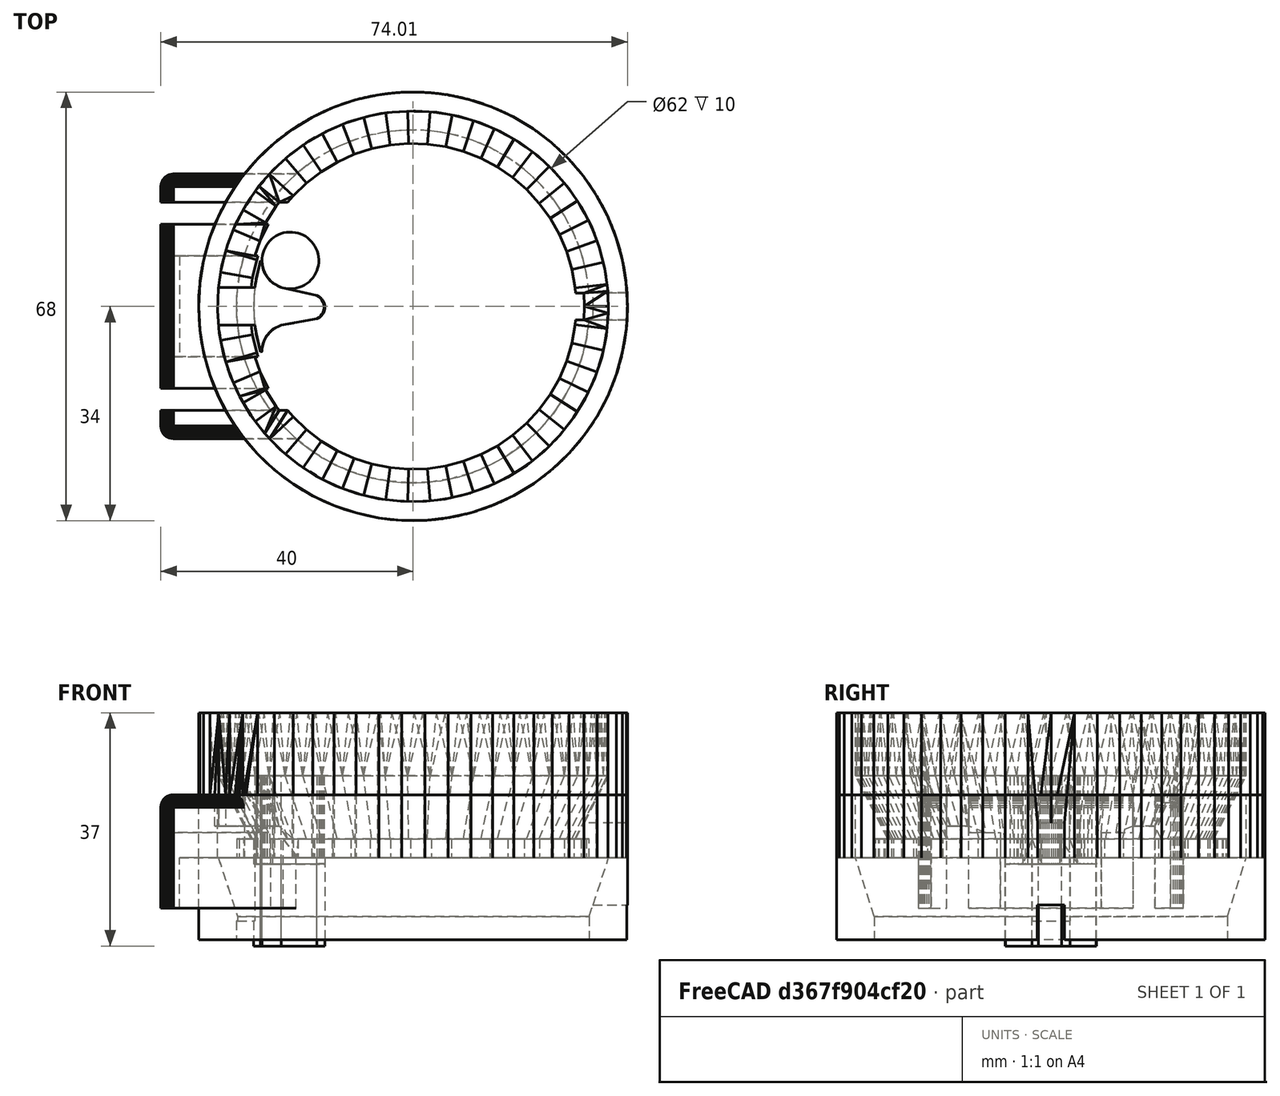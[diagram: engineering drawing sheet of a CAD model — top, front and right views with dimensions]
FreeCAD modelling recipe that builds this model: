
FCSTD DOCUMENT  (FreeCAD 0.20R29177 +426 (Git))
Label: lid
License: All rights reserved
LicenseURL: http://en.wikipedia.org/wiki/All_rights_reserved
objects: Part::MultiFuse×3, Part::Cylinder×3, Part::Cut×3, Part::Box×2, Mesh::Feature×1, Sketcher::SketchObject×1, Part::Extrusion×1, Part::FeaturePython×1, Part::Cone×1, Part::Feature×1
note: 16 computed .brp shape members not serialized (recipe doc carries the construction recipe); baked Part::Feature solids carry a one-line shape summary decoded from their .brp

FEATURE [Mesh::Feature] Lid_V5  label="Lid V5"
FEATURE [Part::Box] Box012  label="Cube012"
  AttacherType = Attacher::AttachEngine3D
  Height = 10
  Length = 10
  Placement = pos=(7,36.17,76) rot=(0,0,1;0rad)
  Width = 6
FEATURE [Sketcher::SketchObject] Sketch
  FullyConstrained = true
  MapMode = 2
  Placement = pos=(0,5,65) rot=(0,0,1;0rad)
  sketch-geometry (8):
    g0: ArcOfCircle CenterX=20.555 CenterY=41.4363 CenterZ=0 NormalX=0 NormalY=0 NormalZ=1 AngleXU=0 Radius=4.5 StartAngle=3.17145 EndAngle=4.38602
    g1: ArcOfCircle CenterX=24.0176 CenterY=34.022 CenterZ=0 NormalX=0 NormalY=0 NormalZ=1 AngleXU=0 Radius=2 StartAngle=5.10518 EndAngle=7.46119
    g2: ArcOfCircle CenterX=20.5312 CenterY=26.882 CenterZ=0 NormalX=0 NormalY=0 NormalZ=1 AngleXU=0 Radius=4.5 StartAngle=1.8916 EndAngle=3.11914
    g3: LineSegment StartX=19.1123 StartY=31.1525 StartZ=0 EndX=24.7831 EndY=32.1743 EndZ=0
    g4: LineSegment StartX=19.1123 StartY=37.1738 StartZ=0 EndX=24.7831 EndY=35.8697 EndZ=0
    g5: LineSegment StartX=16.057 StartY=41.302 StartZ=0 EndX=15.8089 EndY=41.3763 EndZ=0
    g6: LineSegment StartX=15.8133 StartY=26.9187 StartZ=0 EndX=16.0324 EndY=26.9831 EndZ=0
    g7: ArcOfCircle CenterX=39.7432 CenterY=34.1548 CenterZ=0 NormalX=0 NormalY=0 NormalZ=1 AngleXU=0 Radius=25 StartAngle=2.84856 EndAngle=3.43524
  constraints (28):
    c: Coincident(g3,g2)
    c: Coincident(g3,g1)
    c: Coincident(g4,g0)
    c: Coincident(g4,g1)
    c: Coincident(g5,g0)
    c: Coincident(g6,g2)
    c: Coincident(g7,g6)
    c: Coincident(g7,g5)
    c: Radius(g2) = 4.5
    c: Radius(g0) = 4.5
    c: Radius(g1) = 2
    c: Radius(g7) = 25
    c: DistanceX(g5) = 15.8089
    c: DistanceY(g5) = 41.3763
    c: DistanceX(g2) = 16.0324
    c: DistanceY(g2) = 26.9831
    c: DistanceX(g3) = 19.1123
    c: DistanceY(g3) = 31.1525
    c: DistanceX(g2,g0) = 0
    c: DistanceX(g3,g1) = 0
    c: DistanceX(g1) = 24.7831
    c: DistanceY(g1) = 32.1743
    c: DistanceX(g5) = 16.057
    c: DistanceY(g5) = 41.302
    c: DistanceX(g7) = 15.8133
    c: DistanceY(g7) = 26.9187
    c: DistanceY(g1) = 35.8697
    c: DistanceY(g0) = 37.1738
FEATURE [Part::Extrusion] Extrude001
  Base = -> Sketch
  Dir = (0,0,1)
  DirMode = 2
  FaceMakerClass = Part::FaceMakerBullseye
  LengthFwd = 14
  LengthRev = 0
  Placement = pos=(0,0,7) rot=(0,0,1;0rad)
  Solid = true
  Symmetric = false
FEATURE [Part::MultiFuse] Fusion006  label="pellet_sorter"
  Placement = pos=(0,1.5,-19) rot=(0,0,1;0rad)
  Shapes = -> [Box012,Extrude001]
FEATURE [Part::FeaturePython] Tube  # WARN: FeaturePython — macro-defined, semantics opaque (R4)
  AttacherType = Attacher::AttachEngine3D
  Height = 23
  InnerRadius = 31
  OuterRadius = 34
  Placement = pos=(40,40.65,54) rot=(0,0,1;0rad)
FEATURE [Part::Cylinder] Cylinder019
  Angle = 360
  AttacherType = Attacher::AttachEngine3D
  FirstAngle = 0
  Height = 13
  Placement = pos=(40,40.65,54) rot=(0,0,1;0rad)
  Radius = 34
  SecondAngle = 0
FEATURE [Part::Cylinder] Cylinder020
  Angle = 360
  AttacherType = Attacher::AttachEngine3D
  FirstAngle = 0
  Height = 13
  Placement = pos=(40,39.2,54) rot=(0,0,1;0rad)
  Radius = 25
  SecondAngle = 0
FEATURE [Part::MultiFuse] Fusion010
  Shapes = -> [Tube,Cylinder019,Cylinder020]
FEATURE [Part::Cone] Cone
  Angle = 360
  AttacherType = Attacher::AttachEngine3D
  Height = 14
  Placement = pos=(40,40.65,53) rot=(0,0,1;0rad)
  Radius1 = 26.5
  Radius2 = 31
FEATURE [Part::Cut] Cut015
  Base = -> Fusion010
  Tool = -> Cone
FEATURE [Part::Cylinder] Cylinder021
  Angle = 360
  AttacherType = Attacher::AttachEngine3D
  FirstAngle = 0
  Height = 4
  Placement = pos=(40,40.65,54) rot=(0,0,1;0rad)
  Radius = 28
  SecondAngle = 0
FEATURE [Part::Cut] Cut016
  Base = -> Cut015
  Tool = -> Cylinder021
FEATURE [Part::MultiFuse] Fusion011
  Shapes = -> [Fusion006,Cut016]
FEATURE [Part::Box] Box013  label="Cube013"
  AttacherType = Attacher::AttachEngine3D
  Height = 10
  Length = 14
  Placement = pos=(64,38.5,49.5) rot=(0,0,1;0rad)
  Width = 4.3
FEATURE [Part::Cut] Cut017  label="lid"
  Base = -> Fusion011
  Tool = -> Box013
FEATURE [Part::Feature] Lid_V5001_solid  label="Lid(Solid)"
  shape: bbox 74.01 x 67.92 x 31 mm, 1876 faces (baked)
